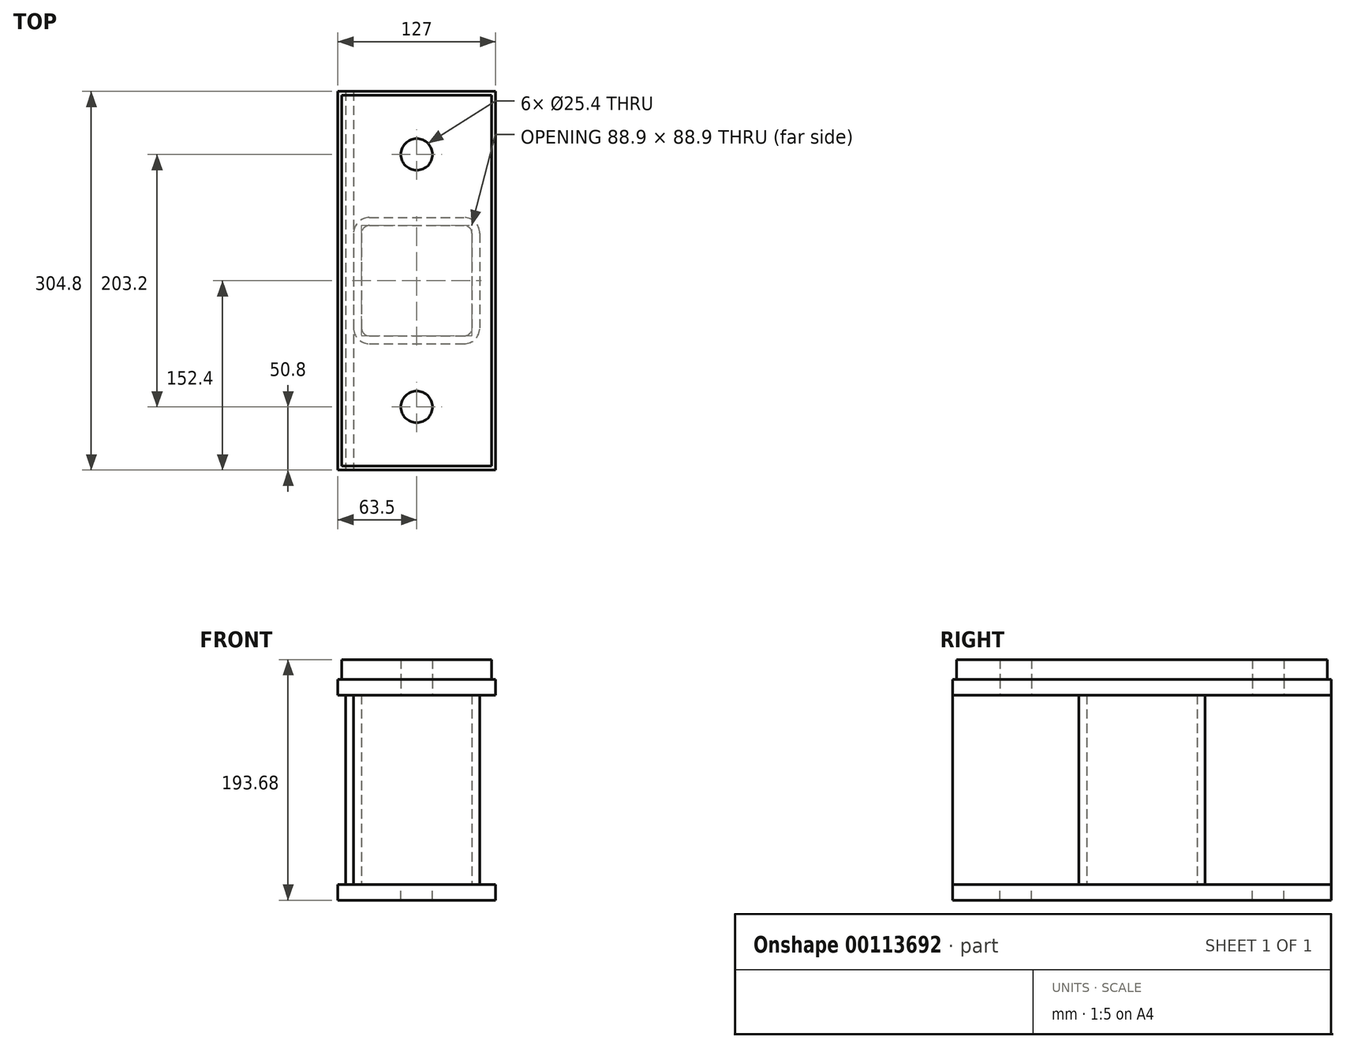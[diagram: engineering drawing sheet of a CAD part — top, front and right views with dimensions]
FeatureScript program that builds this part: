
annotation { "Feature Type Name" : "Feature", "Feature Type Description" : "" }
export const myFeature = defineFeature(function(context is Context, id is Id, definition is map)
    precondition{}
    {
        {
            var Q0;
            Q0=qCreatedBy(makeId("Top.planeOp"),FACE);
            var sketch = newSketch(context, id + "F0", { "sketchPlane" : qUnion([Q0])});
            skLineSegment(sketch, "E0.bottom", {"start": v(-63.5, 152.4) * mm, "end": v(63.5, 152.4) * mm});
            skLineSegment(sketch, "E0.top", {"start": v(-63.5, -152.4) * mm, "end": v(63.5, -152.4) * mm});
            skLineSegment(sketch, "E0.left", {"start": v(-63.5, 152.4) * mm, "end": v(-63.5, -152.4) * mm});
            skLineSegment(sketch, "E0.right", {"start": v(63.5, 152.4) * mm, "end": v(63.5, -152.4) * mm});
            skPoint(sketch, "E0.middle", {"position": v(0, 0) * mm});
            skLineSegment(sketch, "E1", {"start": v(0, 152.4) * mm, "end": v(0, -152.4) * mm, "construction": true});
            skLineSegment(sketch, "E2", {"start": v(-126.12, 0) * mm, "end": v(123.6, 0) * mm, "construction": true});
            skLineSegment(sketch, "E3.0", {"start": v(-126.12, 101.6) * mm, "end": v(123.6, 101.6) * mm, "construction": true});
            skCircle(sketch, "E4", {"center": v(0, 101.6) * mm, "radius": 12.7 * mm});
            skCircle(sketch, "E5.MirrorC", {"center": v(0, -101.6) * mm, "radius": 12.7 * mm});
            skSolve(sketch);
        }
        {
            var Q0;
            Q0 = qSketchRegion(id + "F0", true);
            extrude(context, id + "F1", {"entities" : qUnion([Q0]), "oppositeDirection" : true, "depth" : 12.7 * mm});
        }
        {
            var Q0;
            Q0=makeQuery(id+"F1.opExtrude","CAP_FACE",FACE,{"disambiguationData":[OSD([sQuery(id+"F0.wireOp",EDGE,"E0.bottom"),sQuery(id+"F0.wireOp",EDGE,"E0.top"),sQuery(id+"F0.wireOp",EDGE,"E0.left"),sQuery(id+"F0.wireOp",EDGE,"E0.right"),sQuery(id+"F0.wireOp",EDGE,"E4"),sQuery(id+"F0.wireOp",EDGE,"E5.MirrorC")])],"isStart":true});
            var sketch = newSketch(context, id + "F2", { "sketchPlane" : qUnion([Q0])});
            skLineSegment(sketch, "E6.bottom", {"start": v(-38.1, 50.8) * mm, "end": v(38.1, 50.8) * mm});
            skLineSegment(sketch, "E6.top", {"start": v(-38.1, -50.8) * mm, "end": v(38.1, -50.8) * mm});
            skLineSegment(sketch, "E6.left", {"start": v(-50.8, 38.1) * mm, "end": v(-50.8, -38.1) * mm});
            skLineSegment(sketch, "E6.right", {"start": v(50.8, 38.1) * mm, "end": v(50.8, -38.1) * mm});
            skPoint(sketch, "E6.middle", {"position": v(0, 0) * mm});
            skPoint(sketch, "E7.visualSharp", {"position": v(-50.8, 50.8) * mm});
            skArc(sketch, "E7.filletArc", {"start": v(-38.1, 50.8) * mm, "mid": v(-47.08, 47.08) * mm, "end": v(-50.8, 38.1) * mm});
            skPoint(sketch, "E8.visualSharp", {"position": v(50.8, 50.8) * mm});
            skArc(sketch, "E8.filletArc", {"start": v(50.8, 38.1) * mm, "mid": v(47.08, 47.08) * mm, "end": v(38.1, 50.8) * mm});
            skPoint(sketch, "E9.visualSharp", {"position": v(50.8, -50.8) * mm});
            skArc(sketch, "E9.filletArc", {"start": v(38.1, -50.8) * mm, "mid": v(47.08, -47.08) * mm, "end": v(50.8, -38.1) * mm});
            skPoint(sketch, "E10.visualSharp", {"position": v(-50.8, -50.8) * mm});
            skArc(sketch, "E10.filletArc", {"start": v(-50.8, -38.1) * mm, "mid": v(-47.08, -47.08) * mm, "end": v(-38.1, -50.8) * mm});
            skLineSegment(sketch, "E11.0", {"start": v(-38.1, 44.45) * mm, "end": v(38.1, 44.45) * mm});
            skArc(sketch, "E11.1", {"start": v(44.45, 38.1) * mm, "mid": v(42.6, 42.6) * mm, "end": v(38.1, 44.45) * mm});
            skArc(sketch, "E11.2", {"start": v(-38.1, 44.45) * mm, "mid": v(-42.6, 42.6) * mm, "end": v(-44.45, 38.1) * mm});
            skLineSegment(sketch, "E11.3", {"start": v(44.45, 38.1) * mm, "end": v(44.45, -38.1) * mm});
            skLineSegment(sketch, "E11.4", {"start": v(-44.45, 38.1) * mm, "end": v(-44.45, -38.1) * mm});
            skArc(sketch, "E11.5", {"start": v(-44.45, -38.1) * mm, "mid": v(-42.6, -42.6) * mm, "end": v(-38.1, -44.45) * mm});
            skLineSegment(sketch, "E11.6", {"start": v(-38.1, -44.45) * mm, "end": v(38.1, -44.45) * mm});
            skArc(sketch, "E11.7", {"start": v(38.1, -44.45) * mm, "mid": v(42.6, -42.6) * mm, "end": v(44.45, -38.1) * mm});
            skSolve(sketch);
        }
        {
            var Q0;
            Q0 = qSketchRegion(id + "F2", true);
            extrude(context, id + "F3", {"entities" : qUnion([Q0]), "depth" : 152.4 * mm});
        }
        {
            var Q0;
            Q0=makeQuery(id+"F3.opExtrude","SWEPT_FACE",FACE,{"disambiguationData":[OSD([sQuery(id+"F2.wireOp",EDGE,"E6.left")])]});
            var sketch = newSketch(context, id + "F4", { "sketchPlane" : qUnion([Q0])});
            skLineSegment(sketch, "E12.0", {"start": v(-38.1, 152.4) * mm, "end": v(-38.1, 0) * mm, "construction": true});
            skLineSegment(sketch, "E13", {"start": v(-38.1, 76.2) * mm, "end": v(31.6, 76.2) * mm, "construction": true});
            skSolve(sketch);
        }
        {
            var Q0;
            Q0=makeQuery(id+"F1.opExtrude","CAP_FACE",FACE,{"disambiguationData":[OSD([sQuery(id+"F0.wireOp",EDGE,"E0.bottom"),sQuery(id+"F0.wireOp",EDGE,"E0.top"),sQuery(id+"F0.wireOp",EDGE,"E0.left"),sQuery(id+"F0.wireOp",EDGE,"E0.right"),sQuery(id+"F0.wireOp",EDGE,"E4"),sQuery(id+"F0.wireOp",EDGE,"E5.MirrorC")])],"isStart":true});
            var Q1;
            Q1=makeQuery(id+"F3.opExtrude","CAP_FACE",FACE,{"disambiguationData":[OSD([sQuery(id+"F2.wireOp",EDGE,"E6.bottom"),sQuery(id+"F2.wireOp",EDGE,"E6.top"),sQuery(id+"F2.wireOp",EDGE,"E6.left"),sQuery(id+"F2.wireOp",EDGE,"E6.right"),sQuery(id+"F2.wireOp",EDGE,"E7.filletArc"),sQuery(id+"F2.wireOp",EDGE,"E8.filletArc"),sQuery(id+"F2.wireOp",EDGE,"E9.filletArc"),sQuery(id+"F2.wireOp",EDGE,"E10.filletArc"),sQuery(id+"F2.wireOp",EDGE,"E11.0"),sQuery(id+"F2.wireOp",EDGE,"E11.1"),sQuery(id+"F2.wireOp",EDGE,"E11.2"),sQuery(id+"F2.wireOp",EDGE,"E11.3"),sQuery(id+"F2.wireOp",EDGE,"E11.4"),sQuery(id+"F2.wireOp",EDGE,"E11.5"),sQuery(id+"F2.wireOp",EDGE,"E11.6"),sQuery(id+"F2.wireOp",EDGE,"E11.7")])],"isStart":false});
            cPlane(context, id + "F5", {"entities" : qUnion([Q0, Q1]), "cplaneType" : CPlaneType.MID_PLANE, "offset" : 25.4 * mm, "width" : 152.4 * mm, "height" : 152.4 * mm});
        }
        {
            var Q0;
            Q0=makeQuery(id+"F1.opExtrude","SWEPT_BODY",BODY,{"disambiguationData":[OSD([sQuery(id+"F0.wireOp",EDGE,"E0.bottom"),sQuery(id+"F0.wireOp",EDGE,"E0.top"),sQuery(id+"F0.wireOp",EDGE,"E0.left"),sQuery(id+"F0.wireOp",EDGE,"E0.right"),sQuery(id+"F0.wireOp",EDGE,"E4"),sQuery(id+"F0.wireOp",EDGE,"E5.MirrorC")])]});
            var Q1;
            Q1=qCreatedBy(id+"F5.planeOp",FACE);
            mirror(context, id + "F6", {"entities" : qUnion([Q0]), "mirrorPlane" : qUnion([Q1])});
        }
        {
            var Q0;
            {var subQ0=sQuery(id+"F2.wireOp",EDGE,"E6.left");Q0=makeQuery(id+"F4.imprint","IMPRINT",FACE,{"disambiguationData":[TD([[makeQuery(id+"F4.imprint","IMPRINT",EDGE,{"derivedFrom":makeQuery(id+"F3.opExtrude","CAP_EDGE",EDGE,{"disambiguationData":[OSD([subQ0])],"isStart":true})}),1.0]])]});}
            var sketch = newSketch(context, id + "F7", { "sketchPlane" : qUnion([Q0])});
            skLineSegment(sketch, "E14.0", {"start": v(-152.4, 0) * mm, "end": v(152.4, 0) * mm});
            skLineSegment(sketch, "E15.0", {"start": v(-152.4, 152.4) * mm, "end": v(152.4, 152.4) * mm});
            skLineSegment(sketch, "E16", {"start": v(-152.4, 0) * mm, "end": v(-152.4, 152.4) * mm});
            skLineSegment(sketch, "E17", {"start": v(152.4, 0) * mm, "end": v(152.4, 152.4) * mm});
            skSolve(sketch);
        }
        {
            var Q0;
            Q0 = qSketchRegion(id + "F7", true);
            extrude(context, id + "F8", {"entities" : qUnion([Q0]), "depth" : 6.35 * mm});
        }
        {
            var Q0;
            Q0=makeQuery(id+"F6.opPattern","COPY",FACE,{"derivedFrom":makeQuery(id+"F1.opExtrude","CAP_FACE",FACE,{"disambiguationData":[OSD([sQuery(id+"F0.wireOp",EDGE,"E0.bottom"),sQuery(id+"F0.wireOp",EDGE,"E0.top"),sQuery(id+"F0.wireOp",EDGE,"E0.left"),sQuery(id+"F0.wireOp",EDGE,"E0.right"),sQuery(id+"F0.wireOp",EDGE,"E4"),sQuery(id+"F0.wireOp",EDGE,"E5.MirrorC")])],"isStart":false}),"instanceName":"1"});
            var sketch = newSketch(context, id + "F9", { "sketchPlane" : qUnion([Q0])});
            skLineSegment(sketch, "E18.0.0", {"start": v(63.5, 152.4) * mm, "end": v(-63.5, 152.4) * mm});
            skLineSegment(sketch, "E18.0.2", {"start": v(-63.5, -152.4) * mm, "end": v(63.5, -152.4) * mm});
            skLineSegment(sketch, "E18.0.3", {"start": v(63.5, -152.4) * mm, "end": v(63.5, 152.4) * mm});
            skCircle(sketch, "E19.0", {"center": v(0, 101.6) * mm, "radius": 12.7 * mm});
            skCircle(sketch, "E20.0", {"center": v(0, -101.6) * mm, "radius": 12.7 * mm});
            skLineSegment(sketch, "E21.0", {"start": v(-60.32, 149.22) * mm, "end": v(-60.33, -149.23) * mm});
            skLineSegment(sketch, "E21.1", {"start": v(60.33, 149.22) * mm, "end": v(-60.32, 149.22) * mm});
            skLineSegment(sketch, "E21.2", {"start": v(60.32, -149.23) * mm, "end": v(60.33, 149.22) * mm});
            skLineSegment(sketch, "E21.3", {"start": v(-60.33, -149.23) * mm, "end": v(60.32, -149.23) * mm});
            skSolve(sketch);
        }
        {
            var Q0;
            Q0=makeQuery(id+"F9.imprint","IMPRINT",FACE,{"disambiguationData":[TD([[makeQuery(id+"F9.imprint","IMPRINT",EDGE,{"derivedFrom":sQuery(id+"F9.wireOp",EDGE,"E19.0")}),-1.0]])]});
            var Q1;
            Q1 = qConstructionFilter(qBodyType(qCreatedBy(id + "F9" ,EDGE), BodyType.WIRE), ConstructionObject.NO);
            extrude(context, id + "F10", {"entities" : qUnion([Q0]), "surfaceEntities" : qUnion([Q1]), "depth" : 15.88 * mm});
        }
    });
